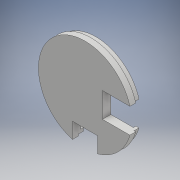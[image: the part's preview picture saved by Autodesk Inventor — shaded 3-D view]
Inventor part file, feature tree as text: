
AUTODESK INVENTOR PART (.ipt)
format: ipt  version: 2018 (Build 220112000, 112)  size: 249,856 bytes
history: native  units: mm
features: extrude x8, sketch x8, fillet x2, pattern_circular x1
ambient origin geometry x8: Origin, YZ Plane, XZ Plane, XY Plane, X Axis, Y Axis, Z Axis, Center Point
bodies: Solid1 (feature_tree)
feature tree (19):
  extrude  "Extrusion1"  Depth=30.0mm
  extrude  "Extrusion4"  TaperAngle=45.0deg  [1 undecoded]
  extrude  "Extrusion3"  Depth=15.0mm
  fillet  "Fillet1"  [1 undecoded]
  extrude  "Extrusion5"  Depth=3.0mm
  extrude  "Extrusion6"  Depth=15.0mm
  extrude  "Extrusion7"  Depth=15.0mm
  fillet  "Fillet2"  [1 undecoded]
  pattern_circular  "Circular Pattern1"  [2 undecoded]
  extrude  "Extrusion8"  Depth=1.0mm
  extrude  "Extrusion9"  Depth=3.5mm
  sketch  "Sketch1"  dims[d0=50.0mm d1=30.0mm]
  sketch  "Sketch3"  dims[d2=15.0mm d3=45.0deg]
  sketch  "Sketch6"  dims[d4=3.0mm d5=15.0mm d6=135.0deg]
  sketch  "Sketch7"  dims[d7=3.0mm d8=54.0mm]
  sketch  "Sketch8"  dims[d9=6.5mm d10=0.0mm d21=15.0mm]
  sketch  "Sketch9"  dims[d22=135.0deg d23=15.0mm d24=45.0deg]
  sketch  "Sketch10"  dims[d25=2.8mm]
  sketch  "Sketch11"  dims[d26=2.8mm d27=2.0mm d28=0.0mm d29=1.0mm d30=50.5mm d31=1.5mm d32=0.0mm d33=27.0mm d34=6.108652mm d35=3.490659mm d36=26.0mm d37=6.108652mm d38=3.490659mm d39=3.0mm d40=0.0mm d41=27.0mm d42=6.981317mm d43=15.0deg d44=26.0mm d45=6.981317mm d46=15.0deg d47=1.5mm d48=0.0mm d49=27.0mm d50=8.901179mm d51=0.174533mm d52=26.0mm d53=8.901179mm d54=0.174533mm d55=0.1mm d56=0.0mm d57=0.3mm d58=20.0mm d59=360.0deg d61=56.0mm d62=3.5mm d63=0.0mm d64=7.5mm d65=10.5mm d66=7.5mm d67=10.5mm d68=17.5mm d69=7.5mm d70=17.5mm d71=7.5mm d72=0.0mm d73=0.0mm]
note: 5 required parameter values undecoded (feature->parameter linkage not recoverable at this tier; creation-order binding heuristic only, values carry confidence <= 0.55)
